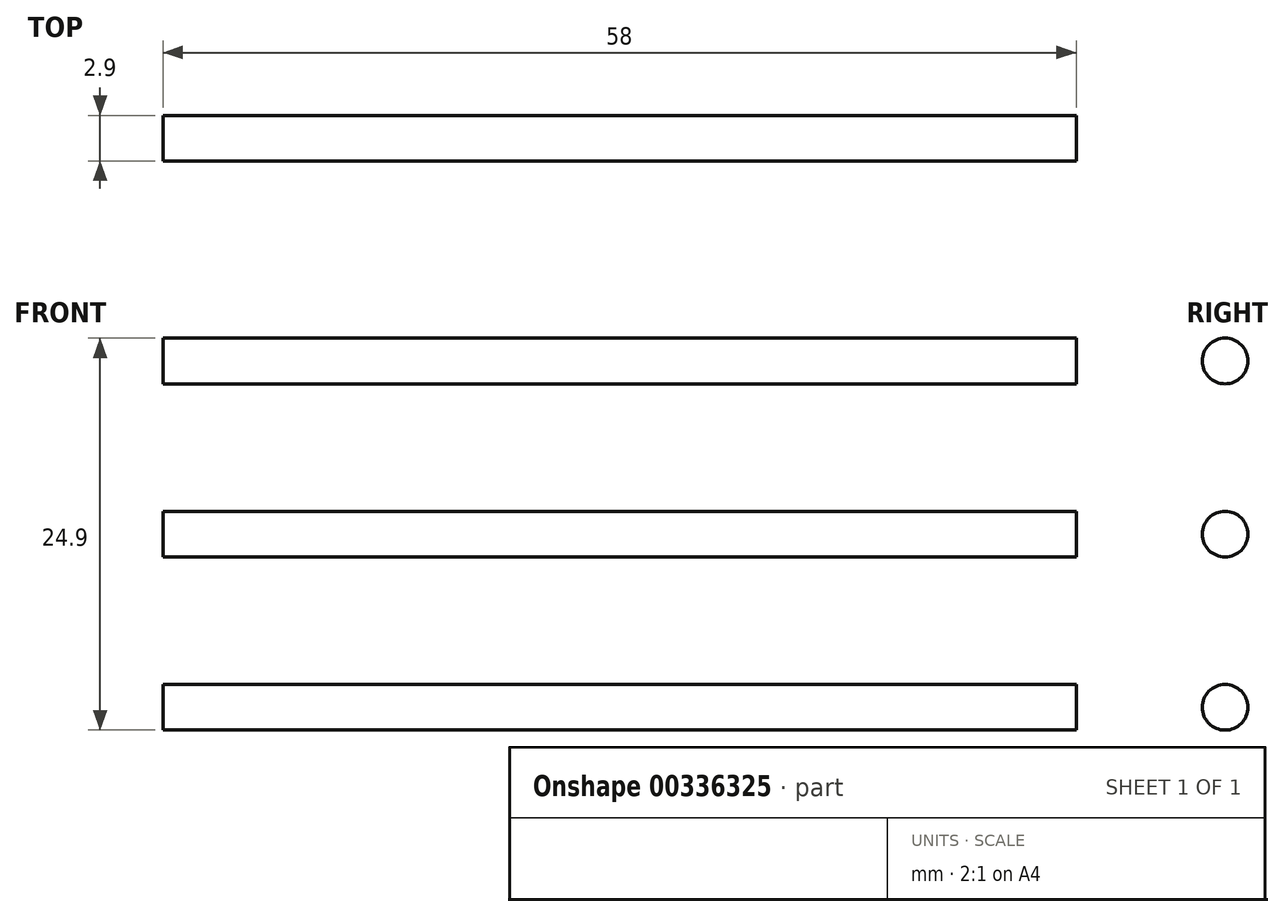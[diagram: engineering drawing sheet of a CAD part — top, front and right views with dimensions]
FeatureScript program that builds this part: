
annotation { "Feature Type Name" : "Feature", "Feature Type Description" : "" }
export const myFeature = defineFeature(function(context is Context, id is Id, definition is map)
    precondition{}
    {
        {
            var Q0;
            Q0=qCreatedBy(makeId("Right.planeOp"),FACE);
            var sketch = newSketch(context, id + "F0", { "sketchPlane" : qUnion([Q0])});
            skCircle(sketch, "E0", {"center": v(0, 22) * mm, "radius": 1.45 * mm});
            skCircle(sketch, "E1", {"center": v(0, 11) * mm, "radius": 1.45 * mm});
            skCircle(sketch, "E2", {"center": v(0, 0) * mm, "radius": 1.45 * mm});
            skSolve(sketch);
        }
        {
            var Q0;
            Q0=makeQuery(id+"F0.imprint","IMPRINT",FACE,{"disambiguationData":[TD([[makeQuery(id+"F0.imprint","IMPRINT",EDGE,{"derivedFrom":sQuery(id+"F0.wireOp",EDGE,"E0")}),1.0]])]});
            var Q1;
            Q1=makeQuery(id+"F0.imprint","IMPRINT",FACE,{"disambiguationData":[TD([[makeQuery(id+"F0.imprint","IMPRINT",EDGE,{"derivedFrom":sQuery(id+"F0.wireOp",EDGE,"E1")}),1.0]])]});
            var Q2;
            Q2=makeQuery(id+"F0.imprint","IMPRINT",FACE,{"disambiguationData":[TD([[makeQuery(id+"F0.imprint","IMPRINT",EDGE,{"derivedFrom":sQuery(id+"F0.wireOp",EDGE,"E2")}),1.0]])]});
            extrude(context, id + "F1", {"entities" : qUnion([Q0, Q1, Q2]), "endBound" : BoundingType.SYMMETRIC, "depth" : 58 * mm});
        }
    });
